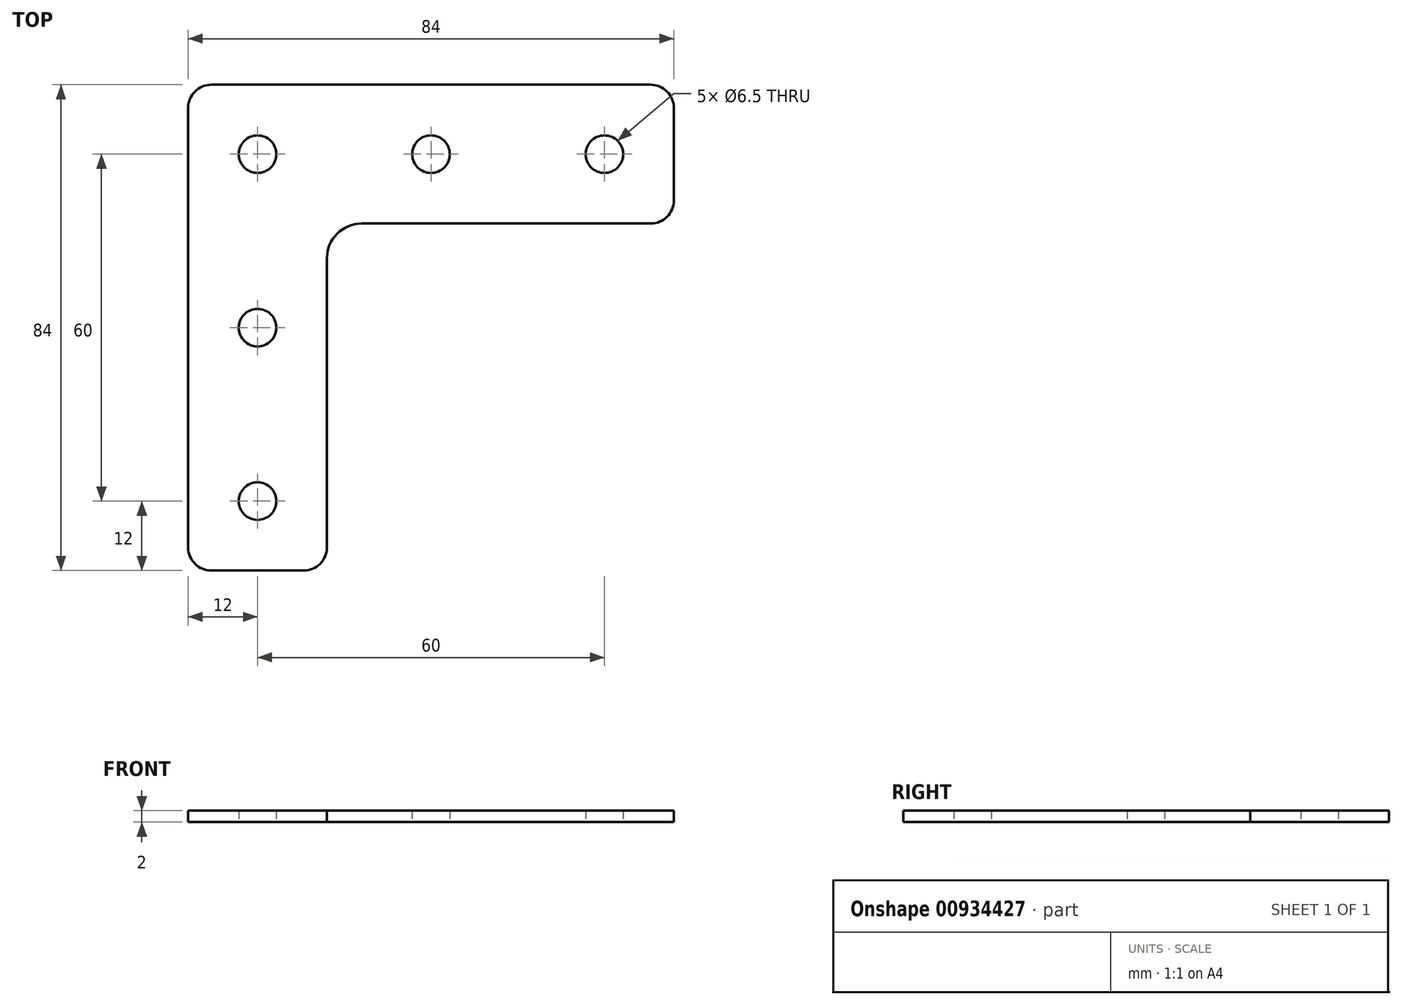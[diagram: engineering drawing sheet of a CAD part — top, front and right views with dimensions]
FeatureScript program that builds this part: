
annotation { "Feature Type Name" : "Feature", "Feature Type Description" : "" }
export const myFeature = defineFeature(function(context is Context, id is Id, definition is map)
    precondition{}
    {
        {
            var Q0;
            Q0=qCreatedBy(makeId("Top.planeOp"),FACE);
            var sketch = newSketch(context, id + "F0", { "sketchPlane" : qUnion([Q0])});
            skLineSegment(sketch, "E0", {"start": v(4, 84) * mm, "end": v(80, 84) * mm});
            skLineSegment(sketch, "E1", {"start": v(84, 80) * mm, "end": v(84, 64) * mm});
            skLineSegment(sketch, "E2", {"start": v(80, 60) * mm, "end": v(30, 60) * mm});
            skLineSegment(sketch, "E3", {"start": v(24, 54) * mm, "end": v(24, 4) * mm});
            skLineSegment(sketch, "E4", {"start": v(20, 0) * mm, "end": v(4, 0) * mm});
            skLineSegment(sketch, "E5", {"start": v(0, 80) * mm, "end": v(0, 4) * mm});
            skCircle(sketch, "E6", {"center": v(12, 12) * mm, "radius": 3.25 * mm});
            skCircle(sketch, "E7", {"center": v(12, 42) * mm, "radius": 3.25 * mm});
            skCircle(sketch, "E8", {"center": v(12, 72) * mm, "radius": 3.25 * mm});
            skCircle(sketch, "E9", {"center": v(42, 72) * mm, "radius": 3.25 * mm});
            skCircle(sketch, "E10", {"center": v(72, 72) * mm, "radius": 3.25 * mm});
            skPoint(sketch, "E11.visualSharp", {"position": v(24, 60) * mm});
            skArc(sketch, "E11.filletArc", {"start": v(30, 60) * mm, "mid": v(25.76, 58.24) * mm, "end": v(24, 54) * mm});
            skPoint(sketch, "E12.visualSharp", {"position": v(84, 60) * mm});
            skArc(sketch, "E12.filletArc", {"start": v(80, 60) * mm, "mid": v(82.83, 61.17) * mm, "end": v(84, 64) * mm});
            skPoint(sketch, "E13.visualSharp", {"position": v(84, 84) * mm});
            skArc(sketch, "E13.filletArc", {"start": v(84, 80) * mm, "mid": v(82.83, 82.83) * mm, "end": v(80, 84) * mm});
            skPoint(sketch, "E14.visualSharp", {"position": v(0, 84) * mm});
            skArc(sketch, "E14.filletArc", {"start": v(4, 84) * mm, "mid": v(1.17, 82.83) * mm, "end": v(0, 80) * mm});
            skPoint(sketch, "E15.visualSharp", {"position": v(0, 0) * mm});
            skArc(sketch, "E15.filletArc", {"start": v(0, 4) * mm, "mid": v(1.17, 1.17) * mm, "end": v(4, 0) * mm});
            skPoint(sketch, "E16.visualSharp", {"position": v(24, 0) * mm});
            skArc(sketch, "E16.filletArc", {"start": v(20, 0) * mm, "mid": v(22.83, 1.17) * mm, "end": v(24, 4) * mm});
            skSolve(sketch);
        }
        {
            var Q0;
            Q0 = qSketchRegion(id + "F0", true);
            extrude(context, id + "F1", {"entities" : qUnion([Q0]), "depth" : 2 * mm, "offsetDistance" : 25 * mm});
        }
    });
